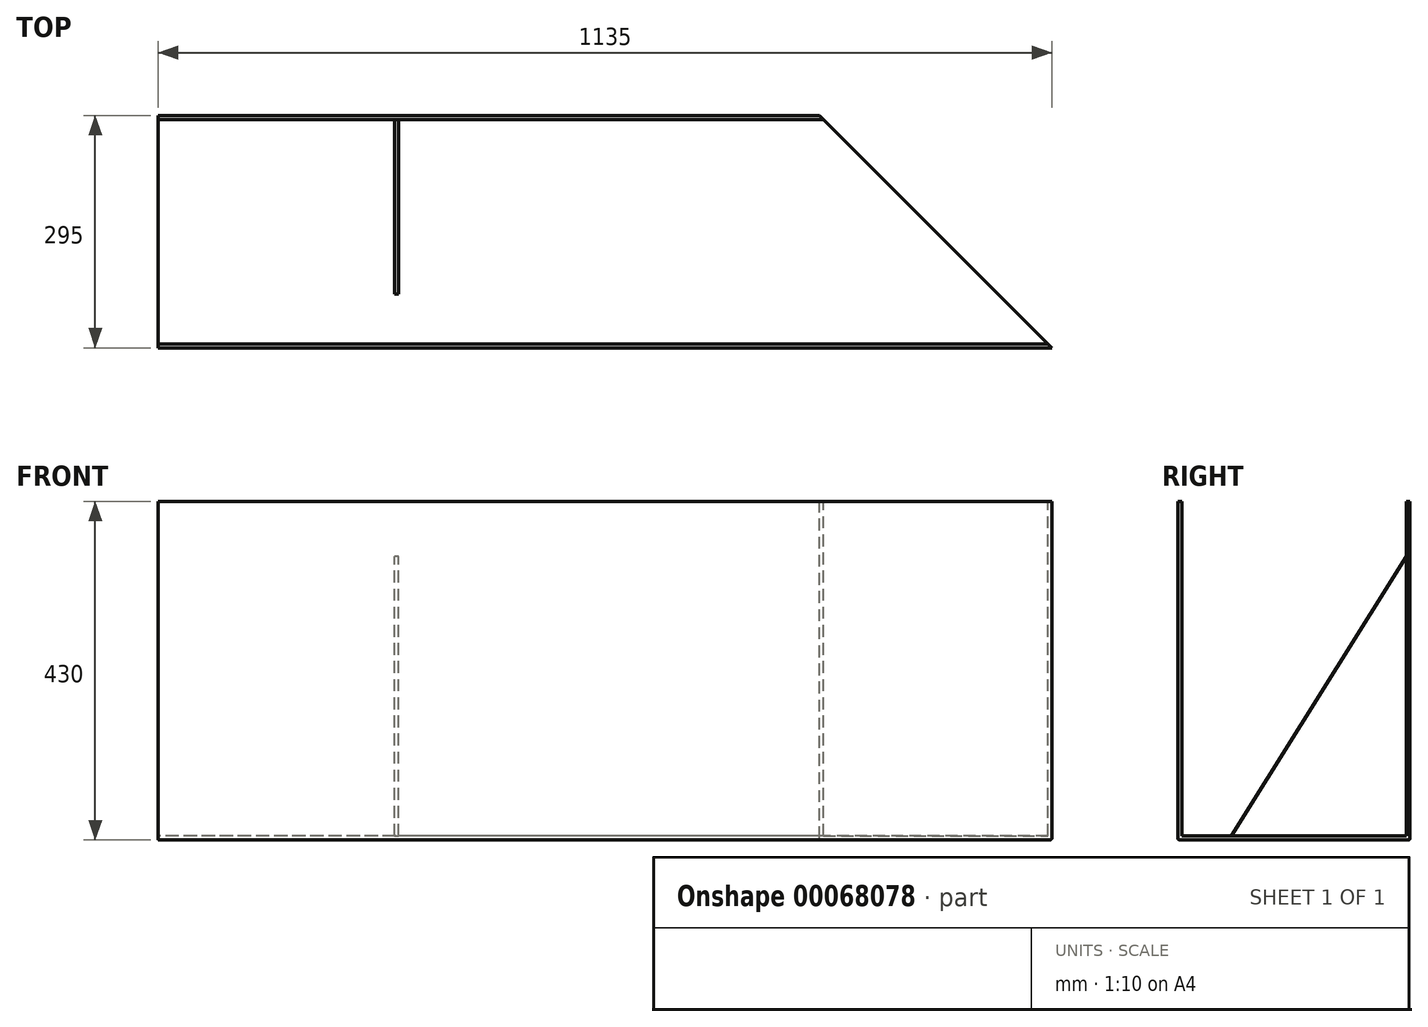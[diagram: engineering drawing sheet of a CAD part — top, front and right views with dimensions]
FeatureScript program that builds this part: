
annotation { "Feature Type Name" : "Feature", "Feature Type Description" : "" }
export const myFeature = defineFeature(function(context is Context, id is Id, definition is map)
    precondition{}
    {
        {
            var Q0;
            Q0=qCreatedBy(makeId("Right.planeOp"),FACE);
            var sketch = newSketch(context, id + "F0", { "sketchPlane" : qUnion([Q0])});
            skLineSegment(sketch, "E0.left", {"start": v(0, 0) * mm, "end": v(0, 430) * mm});
            skLineSegment(sketch, "E1", {"start": v(0, 0) * mm, "end": v(-295, 0) * mm});
            skLineSegment(sketch, "E2", {"start": v(-295, 0) * mm, "end": v(-295, 430) * mm});
            skLineSegment(sketch, "E3.0", {"start": v(-290, 5) * mm, "end": v(-290, 430) * mm});
            skLineSegment(sketch, "E3.1", {"start": v(-5, 5) * mm, "end": v(-290, 5) * mm});
            skLineSegment(sketch, "E3.2", {"start": v(-5, 5) * mm, "end": v(-5, 430) * mm});
            skLineSegment(sketch, "E4", {"start": v(0, 430) * mm, "end": v(-5, 430) * mm});
            skLineSegment(sketch, "E5", {"start": v(-290, 430) * mm, "end": v(-295, 430) * mm});
            skSolve(sketch);
        }
        {
            var Q0;
            Q0=makeQuery(id+"F0.imprint","IMPRINT",FACE,{"disambiguationData":[TD([[makeQuery(id+"F0.imprint","IMPRINT",EDGE,{"derivedFrom":sQuery(id+"F0.wireOp",EDGE,"E0.bottom")}),-1.0]])]});
            var Q1;
            Q1=makeQuery(id+"F0.imprint","IMPRINT",FACE,{"disambiguationData":[TD([[makeQuery(id+"F0.imprint","IMPRINT",EDGE,{"derivedFrom":sQuery(id+"F0.wireOp",EDGE,"E0.left")}),1.0]])]});
            extrude(context, id + "F1", {"entities" : qUnion([Q0, Q1]), "depth" : 1200 * mm});
        }
        {
            var Q0;
            Q0=qCreatedBy(makeId("Right.planeOp"),FACE);
            cPlane(context, id + "F2", {"entities" : qUnion([Q0]), "cplaneType" : CPlaneType.OFFSET, "offset" : 300 * mm, "width" : 150 * mm, "height" : 150 * mm});
        }
        {
            var Q0;
            Q0=qCreatedBy(id+"F2.planeOp",FACE);
            var sketch = newSketch(context, id + "F3", { "sketchPlane" : qUnion([Q0])});
            skLineSegment(sketch, "E6.0", {"start": v(-5, 0) * mm, "end": v(-5, 360) * mm});
            skLineSegment(sketch, "E7.0", {"start": v(-5, 0) * mm, "end": v(-230, 0) * mm});
            skPoint(sketch, "E8", {"position": v(-230, 0) * mm});
            skPoint(sketch, "E9", {"position": v(-5, 360) * mm});
            skLineSegment(sketch, "E10", {"start": v(-5, 360) * mm, "end": v(-230, 0) * mm});
            skSolve(sketch);
        }
        {
            var Q0;
            Q0=makeQuery(id+"F3.imprint","IMPRINT",FACE,{"disambiguationData":[TD([[makeQuery(id+"F3.imprint","IMPRINT",EDGE,{"derivedFrom":sQuery(id+"F3.wireOp",EDGE,"E6.0")}),1.0]])]});
            extrude(context, id + "F4", {"entities" : qUnion([Q0]), "depth" : 5 * mm});
        }
        {
            var Q0;
            Q0=qCreatedBy(makeId("Top.planeOp"),FACE);
            var sketch = newSketch(context, id + "F5", { "sketchPlane" : qUnion([Q0])});
            skLineSegment(sketch, "E11.bottom", {"start": v(0, 0) * mm, "end": v(1200, 0) * mm});
            skLineSegment(sketch, "E11.top", {"start": v(0, -230) * mm, "end": v(1200, -230) * mm});
            skLineSegment(sketch, "E11.left", {"start": v(0, 0) * mm, "end": v(0, -230) * mm});
            skLineSegment(sketch, "E11.right", {"start": v(1200, 0) * mm, "end": v(1200, -230) * mm});
            skSolve(sketch);
        }
        {
            var Q0;
            Q0=makeQuery(id+"F5.imprint","IMPRINT",FACE,{"disambiguationData":[TD([[makeQuery(id+"F5.imprint","IMPRINT",EDGE,{"derivedFrom":sQuery(id+"F5.wireOp",EDGE,"E11.bottom")}),-1.0]])]});
            extrude(context, id + "F6", {"entities" : qUnion([Q0]), "operationType" : NewBodyOperationType.ADD, "depth" : 4 * mm});
        }
        {
            var Q0;
            Q0=makeQuery(id+"F1.opExtrude","SWEPT_EDGE",EDGE,{"disambiguationData":[OSD([sQuery(id+"F0.wireOp",EDGE,"E0.left"),sQuery(id+"F0.wireOp",EDGE,"E1")])]});
            var Q1;
            Q1=makeQuery(id+"F1.opExtrude","SWEPT_EDGE",EDGE,{"disambiguationData":[OSD([sQuery(id+"F0.wireOp",EDGE,"E1"),sQuery(id+"F0.wireOp",EDGE,"E2")])]});
            fillet(context, id + "F7", {"entities" : qUnion([Q0, Q1]), "radius" : 2 * mm, "tangentPropagation" : true, "allowEdgeOverflow" : false});
        }
        {
            var Q0;
            Q0=makeQuery(id+"F1.opExtrude","SWEPT_FACE",FACE,{"disambiguationData":[OSD([sQuery(id+"F0.wireOp",EDGE,"E4")])]});
            var sketch = newSketch(context, id + "F8", { "sketchPlane" : qUnion([Q0])});
            skLineSegment(sketch, "E12", {"start": v(1135, -295) * mm, "end": v(840, 0) * mm});
            skLineSegment(sketch, "E13", {"start": v(1135, -295) * mm, "end": v(1200, -295) * mm});
            skLineSegment(sketch, "E14", {"start": v(1200, -295) * mm, "end": v(1200, 0) * mm});
            skLineSegment(sketch, "E15", {"start": v(1200, 0) * mm, "end": v(840, 0) * mm});
            skLineSegment(sketch, "E16", {"start": v(0, 0) * mm, "end": v(840, 0) * mm, "construction": true});
            skSolve(sketch);
        }
        {
            var Q0;
            Q0=qSketchRegion(id+"F8",true);
            extrude(context, id + "F9", {"entities" : qUnion([Q0]), "operationType" : NewBodyOperationType.REMOVE, "endBound" : BoundingType.THROUGH_ALL, "oppositeDirection" : true, "depth" : 25 * mm});
        }
    });
